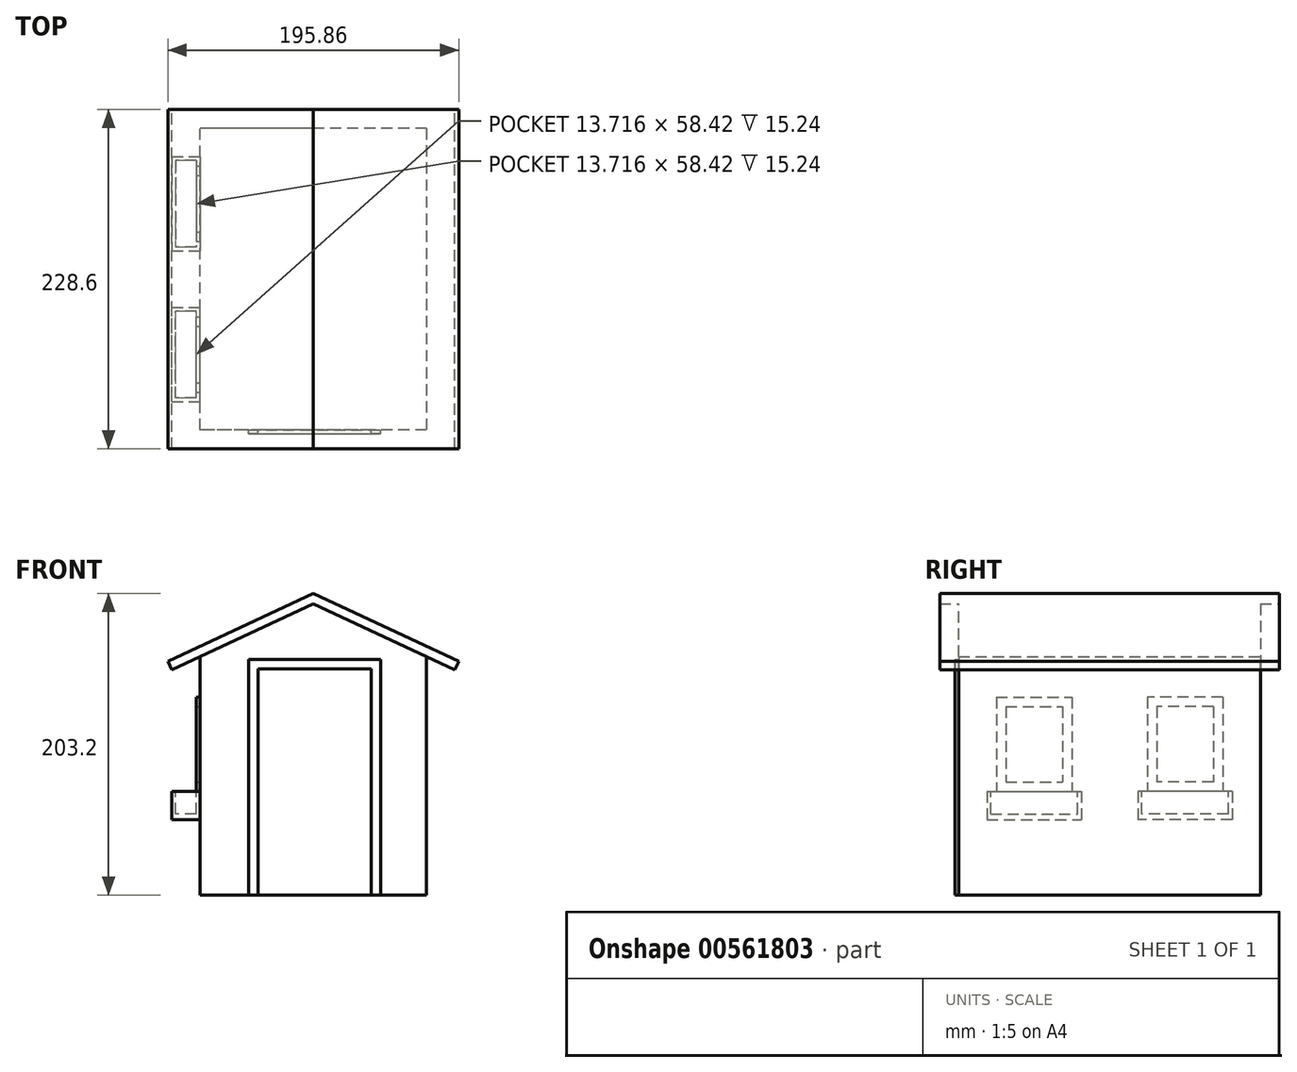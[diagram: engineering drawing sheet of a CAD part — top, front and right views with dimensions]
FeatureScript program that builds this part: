
annotation { "Feature Type Name" : "Feature", "Feature Type Description" : "" }
export const myFeature = defineFeature(function(context is Context, id is Id, definition is map)
    precondition{}
    {
        {
            var Q0;
            Q0=qCreatedBy(makeId("Front.planeOp"),FACE);
            var sketch = newSketch(context, id + "F0", { "sketchPlane" : qUnion([Q0])});
            skLineSegment(sketch, "E0", {"start": v(-76.2, 0) * mm, "end": v(-76.2, 167.67) * mm});
            skLineSegment(sketch, "E1", {"start": v(-76.2, 167.67) * mm, "end": v(0, 203.2) * mm});
            skLineSegment(sketch, "E2", {"start": v(0, 203.2) * mm, "end": v(76.2, 167.67) * mm});
            skLineSegment(sketch, "E3", {"start": v(76.2, 167.67) * mm, "end": v(76.2, 0) * mm});
            skLineSegment(sketch, "E4", {"start": v(76.2, 0) * mm, "end": v(-76.2, 0) * mm});
            skLineSegment(sketch, "E5", {"start": v(0, 53.5) * mm, "end": v(0, -18.92) * mm, "construction": true});
            skSolve(sketch);
        }
        {
            var Q0;
            Q0=makeQuery(id+"F0.imprint","IMPRINT",FACE,{"disambiguationData":[TD([[makeQuery(id+"F0.imprint","IMPRINT",EDGE,{"derivedFrom":sQuery(id+"F0.wireOp",EDGE,"E0")}),-1.0]])]});
            extrude(context, id + "F1", {"entities" : qUnion([Q0]), "endBound" : BoundingType.SYMMETRIC, "depth" : 203.2 * mm, "offsetDistance" : 25.4 * mm});
        }
        {
            var Q0;
            Q0=makeQuery(id+"F1.opExtrude","CAP_FACE",FACE,{"disambiguationData":[OSD([sQuery(id+"F0.wireOp",EDGE,"E0"),sQuery(id+"F0.wireOp",EDGE,"E1"),sQuery(id+"F0.wireOp",EDGE,"E2"),sQuery(id+"F0.wireOp",EDGE,"E3"),sQuery(id+"F0.wireOp",EDGE,"E4")])],"isStart":false});
            var sketch = newSketch(context, id + "F2", { "sketchPlane" : qUnion([Q0])});
            skLineSegment(sketch, "E6.top", {"start": v(-37.12, 152.4) * mm, "end": v(39.08, 152.4) * mm});
            skLineSegment(sketch, "E6.left", {"start": v(-37.12, 0) * mm, "end": v(-37.12, 152.4) * mm});
            skLineSegment(sketch, "E6.right", {"start": v(39.08, 0) * mm, "end": v(39.08, 152.4) * mm});
            skLineSegment(sketch, "E7", {"start": v(-37.12, 0) * mm, "end": v(-43.47, 0) * mm});
            skLineSegment(sketch, "E8", {"start": v(-43.47, 0) * mm, "end": v(-43.47, 158.75) * mm});
            skLineSegment(sketch, "E9", {"start": v(-43.47, 158.75) * mm, "end": v(45.43, 158.75) * mm});
            skLineSegment(sketch, "E10", {"start": v(45.43, 158.75) * mm, "end": v(45.43, 0) * mm});
            skLineSegment(sketch, "E11", {"start": v(45.43, 0) * mm, "end": v(39.08, 0) * mm});
            skSolve(sketch);
        }
        {
            var Q0;
            Q0 = qSketchRegion(id + "F2", true);
            extrude(context, id + "F3", {"entities" : qUnion([Q0]), "operationType" : NewBodyOperationType.ADD, "depth" : 2.54 * mm, "offsetDistance" : 25.4 * mm});
        }
        {
            var Q0;
            Q0=qCreatedBy(makeId("Front.planeOp"),FACE);
            var sketch = newSketch(context, id + "F4", { "sketchPlane" : qUnion([Q0])});
            skLineSegment(sketch, "E12", {"start": v(0, 203.2) * mm, "end": v(-97.93, 157.53) * mm});
            skLineSegment(sketch, "E13", {"start": v(-97.93, 157.53) * mm, "end": v(-95.25, 151.78) * mm});
            skLineSegment(sketch, "E14", {"start": v(-95.25, 151.78) * mm, "end": v(0, 196.2) * mm});
            skLineSegment(sketch, "E15", {"start": v(0, 196.2) * mm, "end": v(95.25, 151.78) * mm});
            skLineSegment(sketch, "E16", {"start": v(95.25, 151.78) * mm, "end": v(97.93, 157.53) * mm});
            skLineSegment(sketch, "E17", {"start": v(97.93, 157.53) * mm, "end": v(0, 203.2) * mm});
            skLineSegment(sketch, "E18", {"start": v(0, -43.34) * mm, "end": v(0, 224.05) * mm, "construction": true});
            skSolve(sketch);
        }
        {
            var Q0;
            Q0 = qSketchRegion(id + "F4", true);
            extrude(context, id + "F5", {"entities" : qUnion([Q0]), "operationType" : NewBodyOperationType.ADD, "endBound" : BoundingType.SYMMETRIC, "depth" : 228.6 * mm, "offsetDistance" : 25.4 * mm});
        }
        {
            var Q0;
            Q0=makeQuery(id+"F1.opExtrude","SWEPT_FACE",FACE,{"disambiguationData":[OSD([sQuery(id+"F0.wireOp",EDGE,"E0")])]});
            var sketch = newSketch(context, id + "F6", { "sketchPlane" : qUnion([Q0])});
            skLineSegment(sketch, "E19.bottom", {"start": v(-76.2, 133.35) * mm, "end": v(-25.4, 133.35) * mm});
            skLineSegment(sketch, "E19.top", {"start": v(-76.2, 69.85) * mm, "end": v(-25.4, 69.85) * mm});
            skLineSegment(sketch, "E19.left", {"start": v(-76.2, 133.35) * mm, "end": v(-76.2, 69.85) * mm});
            skLineSegment(sketch, "E19.right", {"start": v(-25.4, 133.35) * mm, "end": v(-25.4, 69.85) * mm});
            skLineSegment(sketch, "E20.bottom", {"start": v(-69.85, 127) * mm, "end": v(-31.75, 127) * mm});
            skLineSegment(sketch, "E20.top", {"start": v(-69.85, 76.2) * mm, "end": v(-31.75, 76.2) * mm});
            skLineSegment(sketch, "E20.left", {"start": v(-69.85, 127) * mm, "end": v(-69.85, 76.2) * mm});
            skLineSegment(sketch, "E20.right", {"start": v(-31.75, 127) * mm, "end": v(-31.75, 76.2) * mm});
            skLineSegment(sketch, "E21", {"start": v(0, -22.22) * mm, "end": v(0, 215.02) * mm, "construction": true});
            skPoint(sketch, "E21.endSnap0", {"position": v(0, 160.66) * mm});
            skLineSegment(sketch, "E22.MirrorCS", {"start": v(31.75, 127) * mm, "end": v(31.75, 76.2) * mm});
            skLineSegment(sketch, "E23.MirrorCS", {"start": v(69.85, 127) * mm, "end": v(69.85, 76.2) * mm});
            skLineSegment(sketch, "E24.MirrorCS", {"start": v(69.85, 76.2) * mm, "end": v(31.75, 76.2) * mm});
            skLineSegment(sketch, "E25.MirrorCS", {"start": v(69.85, 127) * mm, "end": v(31.75, 127) * mm});
            skLineSegment(sketch, "E26.MirrorCS", {"start": v(76.2, 133.35) * mm, "end": v(25.4, 133.35) * mm});
            skLineSegment(sketch, "E27.MirrorCS", {"start": v(25.4, 133.35) * mm, "end": v(25.4, 69.85) * mm});
            skLineSegment(sketch, "E28.MirrorCS", {"start": v(76.2, 69.85) * mm, "end": v(25.4, 69.85) * mm});
            skLineSegment(sketch, "E29.MirrorCS", {"start": v(76.2, 133.35) * mm, "end": v(76.2, 69.85) * mm});
            skSolve(sketch);
        }
        {
            var Q0;
            Q0 = qSketchRegion(id + "F6", true);
            extrude(context, id + "F7", {"entities" : qUnion([Q0]), "operationType" : NewBodyOperationType.ADD, "depth" : 2.54 * mm, "offsetDistance" : 25.4 * mm});
        }
        {
            var Q0;
            {var subQ0=sQuery(id+"F0.wireOp",EDGE,"E4");var subQ4=sQuery(id+"F0.wireOp",EDGE,"E0");Q0=makeQuery(id+"F7.boolean.opBoolean","SPLIT",FACE,{"disambiguationData":[TD([makeQuery(id+"F1.opExtrude","SWEPT_FACE",FACE,{"disambiguationData":[OSD([subQ0])]})])],"derivedFrom":makeQuery(id+"F1.opExtrude","SWEPT_FACE",FACE,{"disambiguationData":[OSD([subQ4])]})});}
            var sketch = newSketch(context, id + "F8", { "sketchPlane" : qUnion([Q0])});
            skLineSegment(sketch, "E30.bottom", {"start": v(-82.55, 69.85) * mm, "end": v(-19.05, 69.85) * mm});
            skLineSegment(sketch, "E30.top", {"start": v(-82.55, 50.8) * mm, "end": v(-19.05, 50.8) * mm});
            skLineSegment(sketch, "E30.left", {"start": v(-82.55, 69.85) * mm, "end": v(-82.55, 50.8) * mm});
            skLineSegment(sketch, "E30.right", {"start": v(-19.05, 69.85) * mm, "end": v(-19.05, 50.8) * mm});
            skLineSegment(sketch, "E31", {"start": v(0, 0) * mm, "end": v(0, 141.73) * mm, "construction": true});
            skPoint(sketch, "E31.endSnap0", {"position": v(0, 0) * mm});
            skLineSegment(sketch, "E32.MirrorCS", {"start": v(82.55, 69.85) * mm, "end": v(19.05, 69.85) * mm});
            skLineSegment(sketch, "E33.MirrorCS", {"start": v(82.55, 50.8) * mm, "end": v(19.05, 50.8) * mm});
            skLineSegment(sketch, "E34.MirrorCS", {"start": v(19.05, 69.85) * mm, "end": v(19.05, 50.8) * mm});
            skLineSegment(sketch, "E35.MirrorCS", {"start": v(82.55, 69.85) * mm, "end": v(82.55, 50.8) * mm});
            skSolve(sketch);
        }
        {
            var Q0;
            Q0 = qSketchRegion(id + "F8", true);
            extrude(context, id + "F9", {"entities" : qUnion([Q0]), "operationType" : NewBodyOperationType.ADD, "depth" : 19.05 * mm, "offsetDistance" : 25.4 * mm});
        }
        {
            var Q0;
            Q0=makeQuery(id+"F9.opExtrude","SWEPT_FACE",FACE,{"disambiguationData":[OSD([sQuery(id+"F8.wireOp",EDGE,"E30.bottom")])]});
            var sketch = newSketch(context, id + "F10", { "sketchPlane" : qUnion([Q0])});
            skPoint(sketch, "E36.firstSnap0", {"position": v(-75.94, 80.01) * mm});
            skLineSegment(sketch, "E36.bottom", {"start": v(-79, 80.01) * mm, "end": v(-92.7, 80.01) * mm});
            skLineSegment(sketch, "E36.top", {"start": v(-79, 21.6) * mm, "end": v(-92.7, 21.6) * mm});
            skLineSegment(sketch, "E36.left", {"start": v(-79, 80.01) * mm, "end": v(-79, 21.6) * mm});
            skLineSegment(sketch, "E36.right", {"start": v(-92.7, 80.01) * mm, "end": v(-92.7, 21.6) * mm});
            skLineSegment(sketch, "E37", {"start": v(0, 0) * mm, "end": v(-128.88, 0) * mm, "construction": true});
            skLineSegment(sketch, "E38.MirrorCS", {"start": v(-92.7, -80.01) * mm, "end": v(-92.7, -21.6) * mm});
            skLineSegment(sketch, "E39.MirrorCS", {"start": v(-79, -80.01) * mm, "end": v(-79, -21.6) * mm});
            skLineSegment(sketch, "E40.MirrorCS", {"start": v(-79, -21.6) * mm, "end": v(-92.7, -21.6) * mm});
            skLineSegment(sketch, "E41.MirrorCS", {"start": v(-79, -80.01) * mm, "end": v(-92.7, -80.01) * mm});
            skSolve(sketch);
        }
        {
            var Q0;
            Q0 = qSketchRegion(id + "F10", true);
            extrude(context, id + "F11", {"entities" : qUnion([Q0]), "operationType" : NewBodyOperationType.REMOVE, "oppositeDirection" : true, "depth" : 15.24 * mm, "offsetDistance" : 25.4 * mm});
        }
    });
